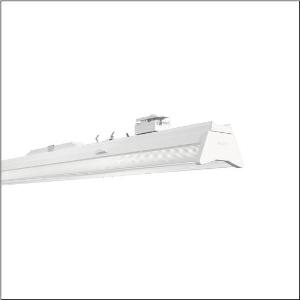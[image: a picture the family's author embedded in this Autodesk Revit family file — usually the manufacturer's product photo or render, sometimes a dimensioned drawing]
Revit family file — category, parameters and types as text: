
# Revit family: licross_r__21_performance_mo_52tm16dn445g_a9c4
name_source: partatom
category: Lighting Fixtures
units: mm (PartAtom-declared; Revit-internal decimal feet)

## family parameters
Cut with Voids When Loaded = No
Host = Face
Light Source = No
Part Type = Normal
Room Calculation Point = No
Round Connector Dimension = Use Diameter
Shared = No

## types (1)
- --- (1 x LED, 4500 lm, 24.9 W, 4000K)
    Apparent Load = 25 VA
    CIE Flux Codes = 66 88 96 79 100
    Color Rendering = 80
    Color Temperature = 4000K
    Default Elevation = 1800 mm
    Description = Licross® 21 Performance MO, luminaire insert, of sheet steel, galvanised, coil coated, white, length: 1.500mm, width: 120mm, height: 123mm, LED rated luminous flux: 4.500lm, light colour: 840, control gear: DALI 2, with plug, 5-pole, with phase selection, mains connection: 220..240V, AC, 50/60Hz, rated input power: 25W, halogen-free wiring, primary light control with lens, of plastic, primary optical cover: cover, of PMMA, CAT 2 (L<= 3000cd/m²), light emission: direct/indirect distribution, primary light characteristic: symmetric, protection rating (complete): IP40, insulation class (complete): insulation class I (protective earthing), certification: CE, ENEC, UKCA, protection symbol: D if used in an environment without relevant dust loads with corresponding accessories, impact resistance: IK06, permissible ambient temperature for indoor applications: -25..+50°C, corresponds to IFS (International Featured Standards) requirements for safety and quality in the food industry, reducing of maximum allowable ambient temperature of 5°C with ceiling mounting, LABS conformity tested according to VDMA 24364:2018-05, packaging unit: 1 piece
    Height = 114 mm
    Lamp = 1 x LED
    Lamp Light Flux = 4500 lm
    Lamp Power = 24.9 W
    Lamp count = 1
    Length = 1500 mm
    Luminous efficacy = 181 lm/W
    Manufacturer = Siteco
    ModVariant = No
    Model = 52TM16DN445G
    Mounting Place = Ceiling
    Mounting Type = Pendant
    Number of Poles = 1
    OnlyDefault = Yes
    Power Factor = 1
    Product Name = Licross® 21 Performance MO
    Product group = luminaire insert
    ProductGroupID = 901
    Protection Class = Protection class I
    Protection Degree = IP 40
    RLX_Detail_Level = 1
    RLX_Emergency_Light_Flux = 0 lm
    RLX_Emergency_Type = 0
    RLX_Emergency_Type_DB = No
    RlxData = <blob elided: 33489 chars, md5=735e6034>
    Socket = socket
    Standby Power = 0 W
    System Light Flux = 4500 lm
    System Power = 25 W
    Type Comments = factory setting: luminous flux: 100 % | dim-lin: 254 | 165 mA
    Type Image = l_1256138.jpg
    URL = http://relux.com
    VarID = @adj_000137
    Voltage = 0 V
    Weight = 0.00 kg
    Width = 120 mm

## geometry (parser evidence)
native form markers: Blend x4, Sweep x12
no freeform markers — native parametric forms only
